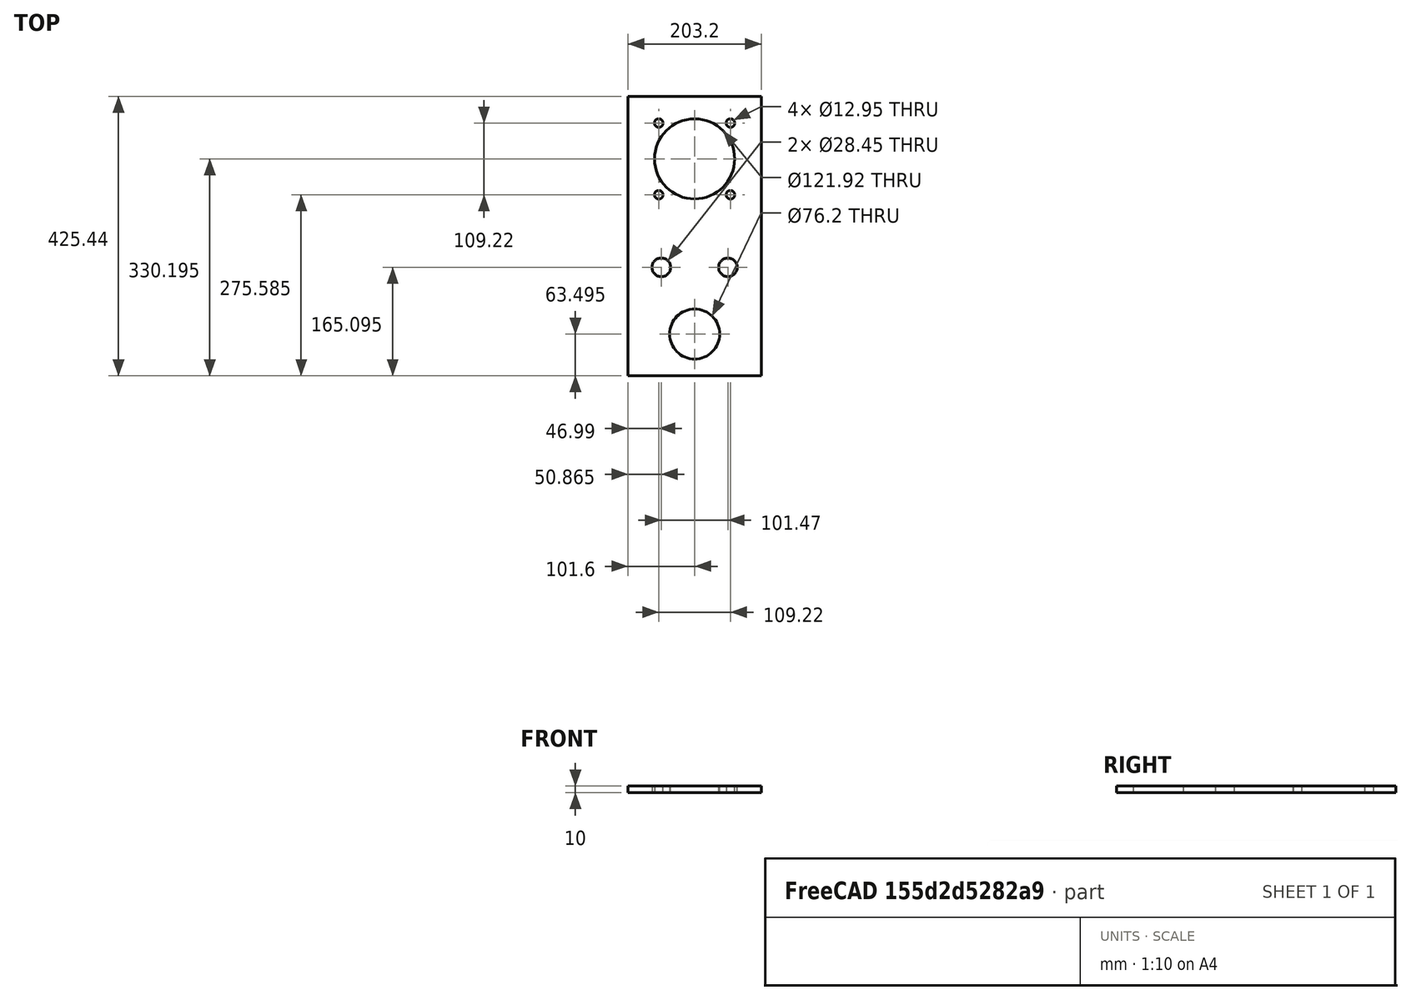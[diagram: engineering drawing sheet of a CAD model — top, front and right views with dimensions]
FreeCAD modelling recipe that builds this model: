
FCSTD DOCUMENT  (FreeCAD 0.16R6712 (Git))
Label: MT_motormountplate
License: All rights reserved
LicenseURL: http://en.wikipedia.org/wiki/All_rights_reserved
objects: Sketcher::SketchObject×1, PartDesign::Pad×1
note: 3 computed .brp shape members not serialized (recipe doc carries the construction recipe); baked Part::Feature solids carry a one-line shape summary decoded from their .brp

FEATURE [Sketcher::SketchObject] Sketch001  label="MM Plate"
  sketch-geometry (13):
    g0: LineSegment StartX=-101.6 StartY=212.725 StartZ=0 EndX=101.6 EndY=212.725 EndZ=0
    g1: LineSegment StartX=101.6 StartY=-212.725 StartZ=0 EndX=-101.6 EndY=-212.725 EndZ=0
    g2: Circle CenterX=0 CenterY=117.475 CenterZ=0 NormalX=0 NormalY=0 NormalZ=1 Radius=60.96
    g3: Circle CenterX=0 CenterY=-149.225 CenterZ=0 NormalX=0 NormalY=0 NormalZ=1 Radius=38.1
    g4: LineSegment StartX=-101.6 StartY=212.725 StartZ=0 EndX=-101.6 EndY=-212.725 EndZ=0
    g5: Circle CenterX=-50.7352 CenterY=-47.625 CenterZ=0 NormalX=0 NormalY=0 NormalZ=1 Radius=14.224
    g6: Circle CenterX=50.7352 CenterY=-47.625 CenterZ=0 NormalX=0 NormalY=0 NormalZ=1 Radius=14.224
    g7: LineSegment StartX=101.6 StartY=212.725 StartZ=0 EndX=101.6 EndY=-212.725 EndZ=0
    g8: Circle CenterX=54.61 CenterY=172.085 CenterZ=0 NormalX=0 NormalY=0 NormalZ=1 Radius=6.477
    g9: Circle CenterX=-54.61 CenterY=172.085 CenterZ=0 NormalX=0 NormalY=0 NormalZ=1 Radius=6.477
    g10: Circle CenterX=54.61 CenterY=62.865 CenterZ=0 NormalX=0 NormalY=0 NormalZ=1 Radius=6.477
    g11: Circle CenterX=-54.61 CenterY=62.865 CenterZ=0 NormalX=0 NormalY=0 NormalZ=1 Radius=6.477
    g12: LineSegment [constr] StartX=-101.6 StartY=117.475 StartZ=0 EndX=101.6 EndY=117.475 EndZ=0
  constraints (37):
    c: Horizontal(g0)
    c: DistanceX(g0,g0) = 203.2
    c: Radius(g2) = 60.96
    c: Radius(g3) = 38.1
    c: Vertical(g4)
    c: Radius(g5) = 14.224
    c: Coincident(g1,g4)
    c: Coincident(g0,g4)
    c: Coincident(g1,g7)
    c: Coincident(g0,g7)
    c: Radius(g8) = 6.477
    c: Symmetric(g9,g8,g-2)
    c: Symmetric(g10,g11,g-2)
    c: PointOnObject(g2,g-2)
    c: Equal(g4,g7)
    c: Symmetric(g6,g5,g-2)
    c: PointOnObject(g3,g-2)
    c: DistanceX(g6) = 50.7352
    c: Equal(g1,g0)
    c: Equal(g4,g7)
    c: DistanceY(g1,g3) = 63.5
    c: DistanceY(g1,g5) = 165.1
    c: DistanceY(g2,g0) = 95.25
    c: PointOnObject(g12,g4)
    c: PointOnObject(g12,g7)
    c: PointOnObject(g2,g12)
    c: Symmetric(g9,g11,g12)
    c: Symmetric(g8,g10,g12)
    c: Equal(g5,g6)
    c: DistanceY(g4,g4) = 425.45
    c: Equal(g9,g11)
    c: Equal(g11,g10)
    c: Equal(g10,g8)
    c: Horizontal(g1)
    c: Symmetric(g1,g0,g-1)
    c: DistanceX(g9,g8) = 109.22
    c: DistanceY(g10,g8) = 109.22
FEATURE [PartDesign::Pad] Pad001  label="Motor Mount plate"
  Length = 10
  Length2 = 100
  Sketch = -> Sketch001
  Type = 0
